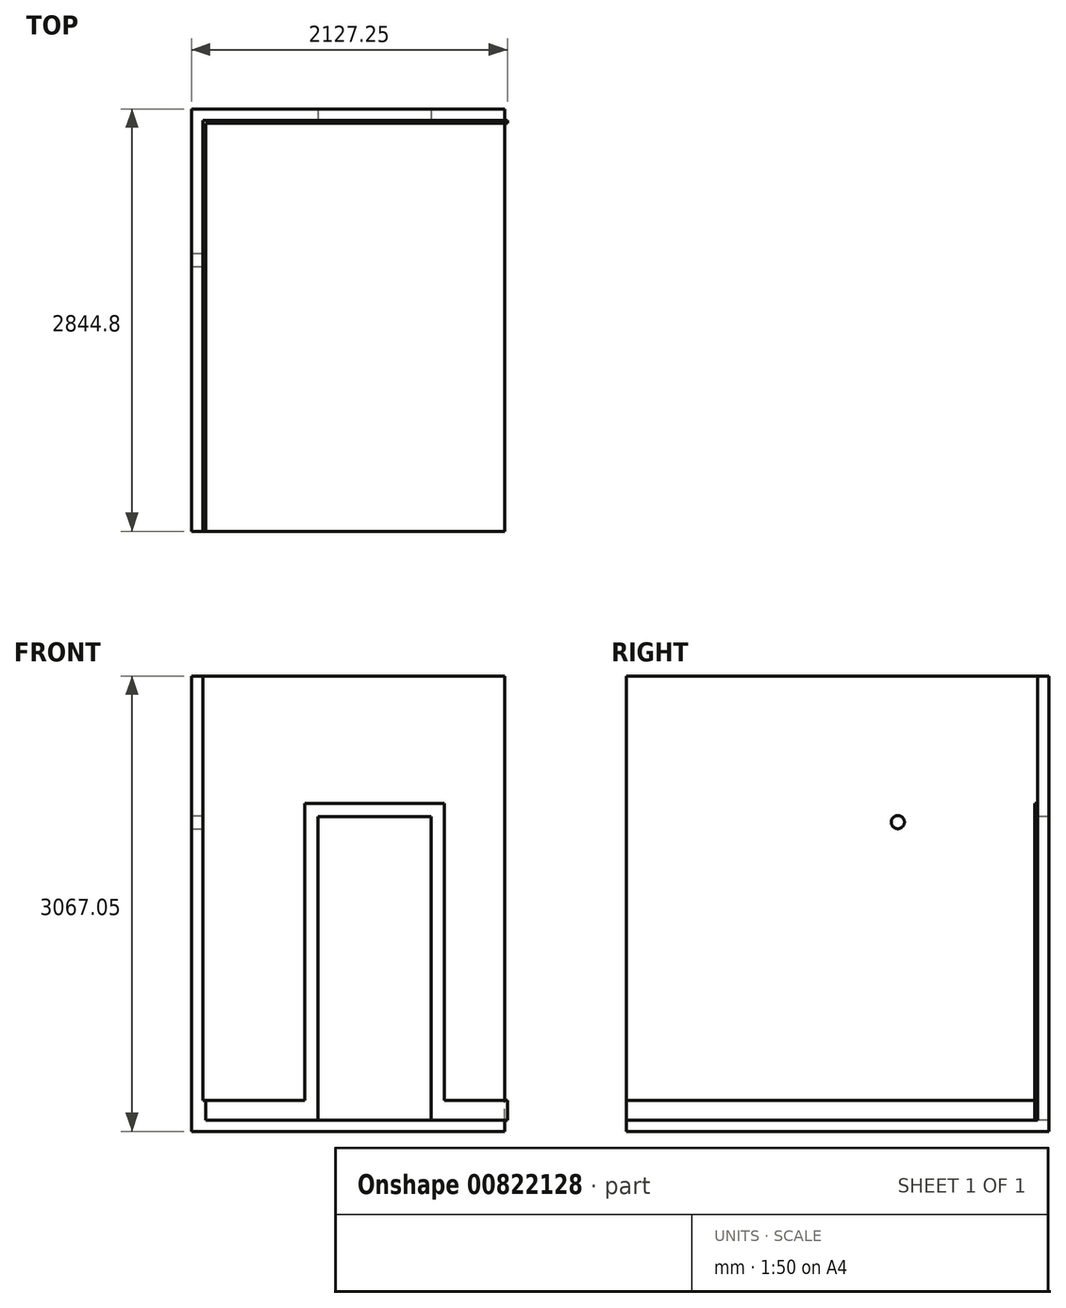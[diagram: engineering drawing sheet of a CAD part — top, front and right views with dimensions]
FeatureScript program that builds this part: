
annotation { "Feature Type Name" : "Feature", "Feature Type Description" : "" }
export const myFeature = defineFeature(function(context is Context, id is Id, definition is map)
    precondition{}
    {
        {
            var Q0;
            Q0=qCreatedBy(makeId("Right.planeOp"),FACE);
            var sketch = newSketch(context, id + "F0", { "sketchPlane" : qUnion([Q0])});
            skLineSegment(sketch, "E0.bottom", {"start": v(0, 0) * mm, "end": v(-2768.6, 0) * mm});
            skLineSegment(sketch, "E0.top", {"start": v(0, 2990.85) * mm, "end": v(-2768.6, 2990.85) * mm});
            skLineSegment(sketch, "E0.left", {"start": v(0, 0) * mm, "end": v(0, 2990.85) * mm});
            skLineSegment(sketch, "E0.right", {"start": v(-2768.6, 0) * mm, "end": v(-2768.6, 2990.85) * mm});
            skSolve(sketch);
        }
        {
            var Q0;
            Q0=makeQuery(id+"F0.imprint","IMPRINT",FACE,{"disambiguationData":[TD([[makeQuery(id+"F0.imprint","IMPRINT",EDGE,{"derivedFrom":sQuery(id+"F0.wireOp",EDGE,"E0.bottom")}),-1.0]])]});
            extrude(context, id + "F1", {"entities" : qUnion([Q0]), "oppositeDirection" : true, "depth" : 76.2 * mm, "offsetDistance" : 25.4 * mm});
        }
        {
            var Q0;
            Q0=makeQuery(id+"F1.opExtrude","SWEPT_FACE",FACE,{"disambiguationData":[OSD([sQuery(id+"F0.wireOp",EDGE,"E0.left")])]});
            var sketch = newSketch(context, id + "F2", { "sketchPlane" : qUnion([Q0])});
            skLineSegment(sketch, "E1.bottom", {"start": v(76.2, 0) * mm, "end": v(-2032, 0) * mm});
            skLineSegment(sketch, "E1.top", {"start": v(76.2, 2990.85) * mm, "end": v(-2032, 2990.85) * mm});
            skLineSegment(sketch, "E1.left", {"start": v(76.2, 0) * mm, "end": v(76.2, 2990.85) * mm});
            skLineSegment(sketch, "E1.right", {"start": v(-2032, 0) * mm, "end": v(-2032, 2990.85) * mm});
            skSolve(sketch);
        }
        {
            var Q0;
            Q0=qSketchRegion(id+"F2",true);
            extrude(context, id + "F3", {"entities" : qUnion([Q0]), "operationType" : NewBodyOperationType.ADD, "depth" : 76.2 * mm, "offsetDistance" : 25.4 * mm});
        }
        {
            var Q0;
            Q0=makeQuery(id+"F3.boolean.opBoolean","MERGE",FACE,{"derivedFrom":[makeQuery(id+"F1.opExtrude","SWEPT_FACE",FACE,{"disambiguationData":[OSD([sQuery(id+"F0.wireOp",EDGE,"E0.bottom")])]}),makeQuery(id+"F3.opExtrude","SWEPT_FACE",FACE,{"disambiguationData":[OSD([sQuery(id+"F2.wireOp",EDGE,"E1.bottom")])]})]});
            var sketch = newSketch(context, id + "F4", { "sketchPlane" : qUnion([Q0])});
            skLineSegment(sketch, "E2.bottom", {"start": v(-76.2, -76.2) * mm, "end": v(2032, -76.2) * mm});
            skLineSegment(sketch, "E2.top", {"start": v(-76.2, 2768.6) * mm, "end": v(2032, 2768.6) * mm});
            skLineSegment(sketch, "E2.left", {"start": v(-76.2, -76.2) * mm, "end": v(-76.2, 2768.6) * mm});
            skLineSegment(sketch, "E2.right", {"start": v(2032, -76.2) * mm, "end": v(2032, 2768.6) * mm});
            skSolve(sketch);
        }
        {
            var Q0;
            Q0=qSketchRegion(id+"F4",true);
            extrude(context, id + "F5", {"entities" : qUnion([Q0]), "operationType" : NewBodyOperationType.ADD, "depth" : 76.2 * mm, "offsetDistance" : 25.4 * mm});
        }
        {
            var Q0;
            Q0=makeQuery(id+"F3.opExtrude","CAP_FACE",FACE,{"disambiguationData":[OSD([sQuery(id+"F2.wireOp",EDGE,"E1.bottom"),sQuery(id+"F2.wireOp",EDGE,"E1.top"),sQuery(id+"F2.wireOp",EDGE,"E1.left"),sQuery(id+"F2.wireOp",EDGE,"E1.right")])],"isStart":true});
            var sketch = newSketch(context, id + "F6", { "sketchPlane" : qUnion([Q0])});
            skPoint(sketch, "E3", {"position": v(774.7, 0) * mm});
            skLineSegment(sketch, "E4.bottom", {"start": v(774.7, 0) * mm, "end": v(1536.7, 0) * mm});
            skLineSegment(sketch, "E4.top", {"start": v(774.7, 2044.7) * mm, "end": v(1536.7, 2044.7) * mm});
            skLineSegment(sketch, "E4.left", {"start": v(774.7, 0) * mm, "end": v(774.7, 2044.7) * mm});
            skLineSegment(sketch, "E4.right", {"start": v(1536.7, 0) * mm, "end": v(1536.7, 2044.7) * mm});
            skSolve(sketch);
        }
        {
            var Q0;
            Q0=makeQuery(id+"F6.imprint","IMPRINT",FACE,{"disambiguationData":[TD([[makeQuery(id+"F6.imprint","IMPRINT",EDGE,{"derivedFrom":sQuery(id+"F6.wireOp",EDGE,"E4.bottom")}),1.0]])]});
            extrude(context, id + "F7", {"entities" : qUnion([Q0]), "operationType" : NewBodyOperationType.REMOVE, "oppositeDirection" : true, "depth" : 76.2 * mm, "offsetDistance" : 25.4 * mm});
        }
        {
            var Q0;
            Q0=makeQuery(id+"F5.boolean.opBoolean","MERGE",FACE,{"derivedFrom":[makeQuery(id+"F1.opExtrude","SWEPT_FACE",FACE,{"disambiguationData":[OSD([sQuery(id+"F0.wireOp",EDGE,"E0.right")])]}),makeQuery(id+"F5.opExtrude","SWEPT_FACE",FACE,{"disambiguationData":[OSD([sQuery(id+"F4.wireOp",EDGE,"E2.top")])]})]});
            var sketch = newSketch(context, id + "F8", { "sketchPlane" : qUnion([Q0])});
            skLineSegment(sketch, "E5.bottom", {"start": v(0, 0) * mm, "end": v(19.05, 0) * mm});
            skLineSegment(sketch, "E5.top", {"start": v(0, 133.35) * mm, "end": v(19.05, 133.35) * mm});
            skLineSegment(sketch, "E5.left", {"start": v(0, 0) * mm, "end": v(0, 133.35) * mm});
            skLineSegment(sketch, "E5.right", {"start": v(19.05, 0) * mm, "end": v(19.05, 133.35) * mm});
            skSolve(sketch);
        }
        {
            var Q0;
            Q0=makeQuery(id+"F8.imprint","IMPRINT",FACE,{"disambiguationData":[TD([[makeQuery(id+"F8.imprint","IMPRINT",EDGE,{"derivedFrom":sQuery(id+"F8.wireOp",EDGE,"E5.bottom")}),1.0]])]});
            extrude(context, id + "F9", {"entities" : qUnion([Q0]), "operationType" : NewBodyOperationType.ADD, "oppositeDirection" : true, "depth" : 2768.6 * mm, "offsetDistance" : 25.4 * mm});
        }
        {
            var Q0;
            Q0=makeQuery(id+"F9.opExtrude","SWEPT_FACE",FACE,{"disambiguationData":[OSD([sQuery(id+"F8.wireOp",EDGE,"E5.right")])]});
            var sketch = newSketch(context, id + "F10", { "sketchPlane" : qUnion([Q0])});
            skLineSegment(sketch, "E6.bottom", {"start": v(0, 0) * mm, "end": v(-19.05, 0) * mm});
            skLineSegment(sketch, "E6.top", {"start": v(0, 133.35) * mm, "end": v(-19.05, 133.35) * mm});
            skLineSegment(sketch, "E6.left", {"start": v(0, 0) * mm, "end": v(0, 133.35) * mm});
            skLineSegment(sketch, "E6.right", {"start": v(-19.05, 0) * mm, "end": v(-19.05, 133.35) * mm});
            skSolve(sketch);
        }
        {
            var Q0;
            Q0=makeQuery(id+"F10.imprint","IMPRINT",FACE,{"disambiguationData":[TD([[makeQuery(id+"F10.imprint","IMPRINT",EDGE,{"derivedFrom":sQuery(id+"F10.wireOp",EDGE,"E6.bottom")}),-1.0]])]});
            extrude(context, id + "F11", {"entities" : qUnion([Q0]), "operationType" : NewBodyOperationType.ADD, "depth" : 2032 * mm, "offsetDistance" : 25.4 * mm});
        }
        {
            var Q0;
            Q0=makeQuery(id+"F11.boolean.opBoolean","MERGE",FACE,{"derivedFrom":[makeQuery(id+"F9.opExtrude","SWEPT_FACE",FACE,{"disambiguationData":[OSD([sQuery(id+"F8.wireOp",EDGE,"E5.top")])]}),makeQuery(id+"F11.opExtrude","SWEPT_FACE",FACE,{"disambiguationData":[OSD([sQuery(id+"F10.wireOp",EDGE,"E6.top")])]})]});
            var sketch = newSketch(context, id + "F12", { "sketchPlane" : qUnion([Q0])});
            skPoint(sketch, "E7", {"position": v(685.8, 0) * mm});
            skLineSegment(sketch, "E8.bottom", {"start": v(685.8, 0) * mm, "end": v(1625.6, 0) * mm});
            skLineSegment(sketch, "E8.top", {"start": v(685.8, -19.05) * mm, "end": v(1625.6, -19.05) * mm});
            skLineSegment(sketch, "E8.left", {"start": v(685.8, 0) * mm, "end": v(685.8, -19.05) * mm});
            skLineSegment(sketch, "E8.right", {"start": v(1625.6, 0) * mm, "end": v(1625.6, -19.05) * mm});
            skSolve(sketch);
        }
        {
            var Q0;
            Q0=qSketchRegion(id+"F12",true);
            extrude(context, id + "F13", {"entities" : qUnion([Q0]), "operationType" : NewBodyOperationType.ADD, "depth" : 2000.25 * mm, "offsetDistance" : 25.4 * mm});
        }
        {
            var Q0;
            Q0=qSketchRegion(id+"F6",true);
            extrude(context, id + "F14", {"entities" : qUnion([Q0]), "operationType" : NewBodyOperationType.REMOVE, "depth" : 19.05 * mm, "offsetDistance" : 25.4 * mm});
        }
        {
            var Q0;
            Q0=makeQuery(id+"F1.opExtrude","CAP_FACE",FACE,{"disambiguationData":[OSD([sQuery(id+"F0.wireOp",EDGE,"E0.bottom"),sQuery(id+"F0.wireOp",EDGE,"E0.top"),sQuery(id+"F0.wireOp",EDGE,"E0.left"),sQuery(id+"F0.wireOp",EDGE,"E0.right")])],"isStart":true});
            var sketch = newSketch(context, id + "F15", { "sketchPlane" : qUnion([Q0])});
            skCircle(sketch, "E9", {"center": v(-939.8, 2006.6) * mm, "radius": 44.45 * mm});
            skSolve(sketch);
        }
        {
            var Q0;
            Q0=makeQuery(id+"F15.imprint","IMPRINT",FACE,{"disambiguationData":[TD([[makeQuery(id+"F15.imprint","IMPRINT",EDGE,{"derivedFrom":sQuery(id+"F15.wireOp",EDGE,"E9")}),1.0]])]});
            extrude(context, id + "F16", {"entities" : qUnion([Q0]), "operationType" : NewBodyOperationType.REMOVE, "oppositeDirection" : true, "depth" : 76.2 * mm, "offsetDistance" : 25.4 * mm});
        }
    });
